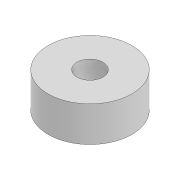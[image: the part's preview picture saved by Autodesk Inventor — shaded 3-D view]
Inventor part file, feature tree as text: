
AUTODESK INVENTOR PART (.ipt)
format: ipt  version: 2022 (Build 260153000, 153)  size: 83,456 bytes
history: native  units: mm
features: extrude x1, sketch x1
ambient origin geometry x8: Origin, YZ Plane, XZ Plane, XY Plane, X Axis, Y Axis, Z Axis, Center Point
bodies: Solid1 (feature_tree)
feature tree (2):
  extrude  "Extrusion1"  Depth=10.0mm
  sketch  "Sketch1"  dims[d0=3.1mm d1=10.0mm d2=4.2mm d3=0.0mm]
